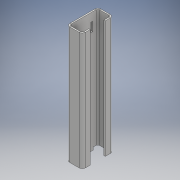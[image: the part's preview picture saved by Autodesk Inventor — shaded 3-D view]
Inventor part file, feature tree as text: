
AUTODESK INVENTOR PART (.ipt)
format: ipt  version: 2017 (Build 210142000, 142)  size: 203,776 bytes
history: native  units: mm
features: sheet_metal_op x5, projected_geometry x4, sketch x3, other x3
ambient origin geometry x8: Origin, YZ Plane, XZ Plane, XY Plane, X Axis, Y Axis, Z Axis, Center Point
bodies: Solid1 (feature_tree)
feature tree (15):
  sheet_metal_op  "Contour Flange1"
  sheet_metal_op  "Face1"
  sketch  "Sketch1"  dims[d0=64.0mm]
  other  "Plate1"
  sheet_metal_op  "Bend1"
  sheet_metal_op  "Corner1"
  sketch  "Sketch2"  dims[d1=29.0mm]
  projected_geometry  "Projected Loop1"
  projected_geometry  "Projected Loop2"
  projected_geometry  "Projected Loop3"
  other  "Plate2"
  sheet_metal_op  "Bend2"
  sketch  "Sketch3"  dims[d2=29.0mm d3=3.0mm d4=1.5mm d5=6.0mm d6=3.9mm d8=3.9mm d9=0.5mm d10=12.0mm d11=3.0mm d12=3.9mm d13=15.0mm d14=15.0mm d15=6.0mm d16=10.0mm d17=10.0mm d18=3.9mm d19=3.0mm d20=1.5mm d21=6.0mm d22=3.9mm d33=20.5mm d34=20.5mm d35=4.0mm d36=4.0mm d37=33.0mm d38=16.5mm d40=9.0mm d41=4.0mm d42=3.0mm d43=0.0mm]
  projected_geometry  "Projected Loop4"
  other  "Cut1"
